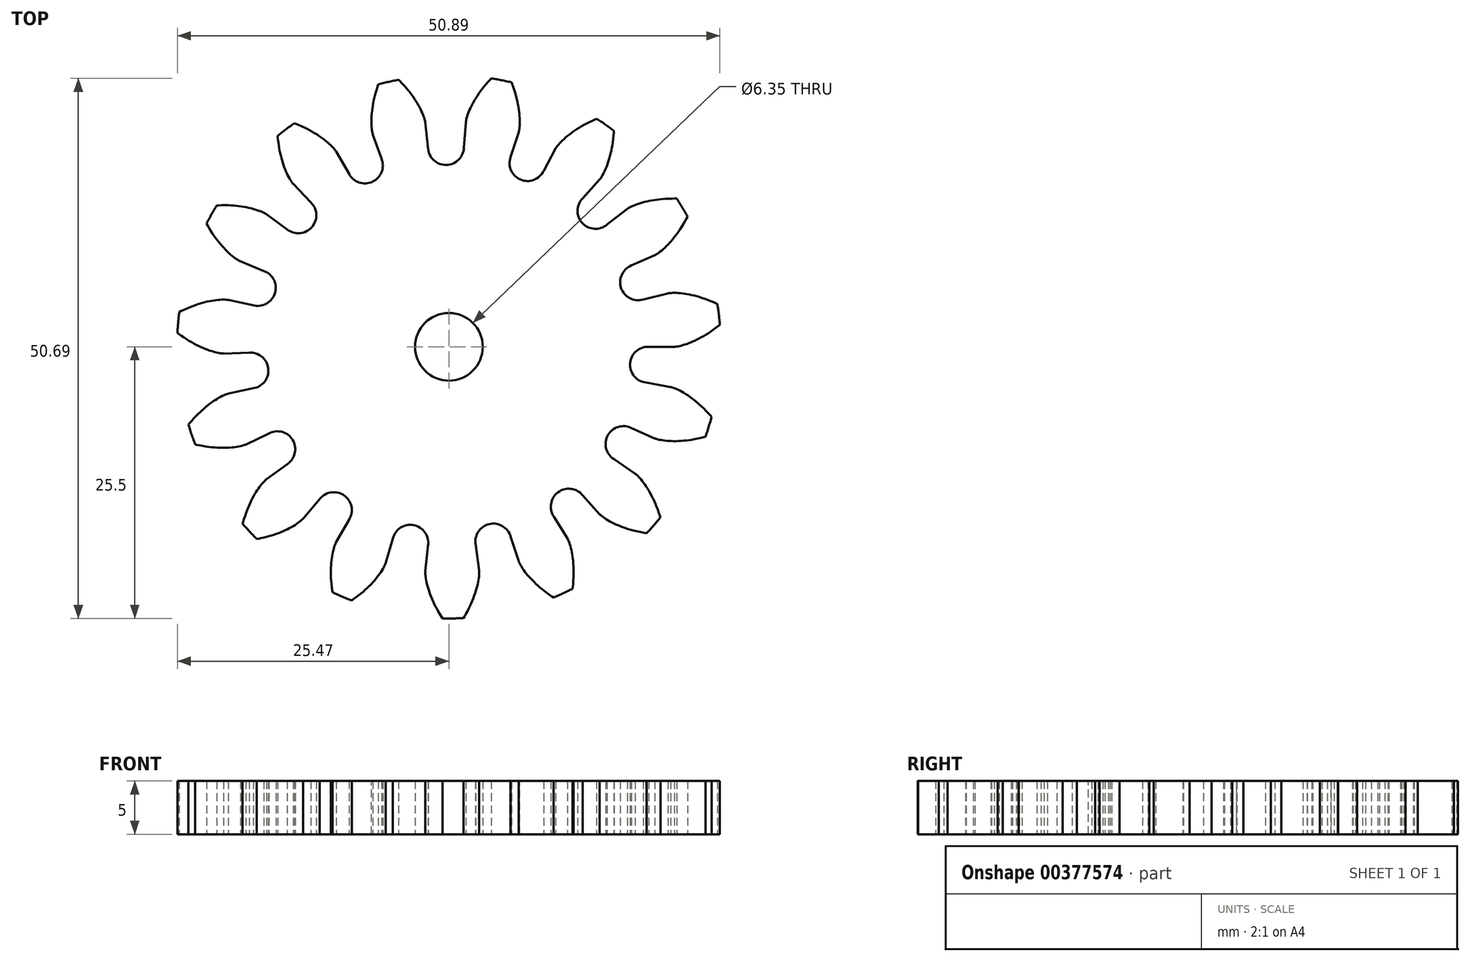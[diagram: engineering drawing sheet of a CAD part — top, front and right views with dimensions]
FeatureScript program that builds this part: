
annotation { "Feature Type Name" : "Feature", "Feature Type Description" : "" }
export const myFeature = defineFeature(function(context is Context, id is Id, definition is map)
    precondition{}
    {
        {
            assignVariable(context, id + "F0", {"name" : "T", "anyValue" : 15});
        }
        {
            var Q0;
            Q0=qCreatedBy(makeId("Top.planeOp"),FACE);
            var sketch = newSketch(context, id + "F1", { "sketchPlane" : qUnion([Q0])});
            skCircle(sketch, "E0", {"center": v(0, 0) * mm, "radius": 25.5 * mm});
            skCircle(sketch, "E1", {"center": v(0, 0) * mm, "radius": 22.5 * mm, "construction": true});
            skCircle(sketch, "E2", {"center": v(0, 0) * mm, "radius": 21.14 * mm, "construction": true});
            skCircle(sketch, "E3", {"center": v(0, 0) * mm, "radius": 18.75 * mm});
            skLineSegment(sketch, "E4", {"start": v(0, 0) * mm, "end": v(21.14, 0) * mm});
            skFitSpline(sketch, "E5", {"points": [v(21.14, 0) * mm, v(21.2, 0) * mm, v(21.38, 0.02) * mm, v(21.67, 0.08) * mm, v(22.07, 0.19) * mm, v(22.57, 0.36) * mm, v(23.17, 0.62) * mm, v(23.85, 0.98) * mm, v(24.6, 1.46) * mm, v(25.4, 2.06) * mm, v(26.26, 2.79) * mm], "startDerivative": vector(5.3, 0.26) * mm, "endDerivative": vector(17.52, 15.1) * mm});
            skLineSegment(sketch, "E6", {"start": v(0, 0) * mm, "end": v(25.4, -2.29) * mm, "construction": true});
            skLineSegment(sketch, "E7", {"start": v(0, 0) * mm, "end": v(22.5, 0.34) * mm, "construction": true});
            skFitSpline(sketch, "E8.MirrorCS", {"points": [v(20.8, -3.78) * mm, v(20.86, -3.8) * mm, v(21.03, -3.84) * mm, v(21.3, -3.95) * mm, v(21.68, -4.13) * mm, v(22.14, -4.4) * mm, v(22.68, -4.75) * mm, v(23.29, -5.23) * mm, v(23.94, -5.83) * mm, v(24.63, -6.56) * mm, v(25.34, -7.44) * mm], "startDerivative": vector(5.17, -1.2) * mm, "endDerivative": vector(14.54, -17.99) * mm});
            skLineSegment(sketch, "E9", {"start": v(0, 0) * mm, "end": v(20.8, -3.78) * mm});
            skSolve(sketch);
        }
        {
            var Q0;
            Q0=qCreatedBy(makeId("Top.planeOp"),FACE);
            var sketch = newSketch(context, id + "F2", { "sketchPlane" : qUnion([Q0])});
            skCircle(sketch, "E10", {"center": v(0, 0) * mm, "radius": 25.5 * mm});
            skSolve(sketch);
        }
        {
            var Q0;
            {var subQ0=sQuery(id+"F1.wireOp",EDGE,"E5");var subQ7=sQuery(id+"F1.wireOp",EDGE,"E0");var subQ8=makeQuery(id+"F1.imprint","INTERSECT",VERTEX,{"derivedFrom":[subQ7,subQ0]});Q0=makeQuery(id+"F1.imprint","IMPRINT",FACE,{"disambiguationData":[TD([[makeQuery(id+"F1.imprint","IMPRINT",EDGE,{"disambiguationData":[TD([[subQ8,1.0]])],"derivedFrom":subQ7}),1.0]])]});}
            extrude(context, id + "F3", {"entities" : qUnion([Q0]), "depth" : 6 * mm});
        }
        {
            var Q0;
            Q0=makeQuery(id+"F3.opExtrude","CAP_FACE",FACE,{"disambiguationData":[OSD([sQuery(id+"F1.wireOp",EDGE,"E0"),sQuery(id+"F1.wireOp",EDGE,"E3"),sQuery(id+"F1.wireOp",EDGE,"E4"),sQuery(id+"F1.wireOp",EDGE,"E5"),sQuery(id+"F1.wireOp",EDGE,"E8.MirrorCS"),sQuery(id+"F1.wireOp",EDGE,"E9")])],"isStart":true});
            var sketch = newSketch(context, id + "F4", { "sketchPlane" : qUnion([Q0])});
            skCircle(sketch, "E11", {"center": v(18.67, 1.68) * mm, "radius": 1.68 * mm});
            skSolve(sketch);
        }
        {
            var Q0;
            {var subQ1=makeQuery(id+"F3.opExtrude","CAP_EDGE",EDGE,{"disambiguationData":[OSD([sQuery(id+"F1.wireOp",EDGE,"E3")])],"isStart":true});Q0=makeQuery(id+"F4.imprint","IMPRINT",FACE,{"disambiguationData":[TD([[makeQuery(id+"F4.imprint","IMPRINT",EDGE,{"derivedFrom":subQ1}),-1.0]])]});}
            extrude(context, id + "F5", {"entities" : qUnion([Q0]), "operationType" : NewBodyOperationType.ADD, "oppositeDirection" : true, "depth" : 6 * mm});
        }
        {
            var Q0;
            Q0=makeQuery(id+"F2.imprint","IMPRINT",FACE,{"disambiguationData":[TD([[makeQuery(id+"F2.imprint","IMPRINT",EDGE,{"derivedFrom":sQuery(id+"F2.wireOp",EDGE,"E10")}),1.0]])]});
            extrude(context, id + "F6", {"entities" : qUnion([Q0]), "depth" : 5 * mm});
        }
        {
            var Q0;
            Q0=makeQuery(id+"F3.opExtrude","SWEPT_BODY",BODY,{"disambiguationData":[OSD([sQuery(id+"F1.wireOp",EDGE,"E0"),sQuery(id+"F1.wireOp",EDGE,"E3"),sQuery(id+"F1.wireOp",EDGE,"E4"),sQuery(id+"F1.wireOp",EDGE,"E5"),sQuery(id+"F1.wireOp",EDGE,"E8.MirrorCS"),sQuery(id+"F1.wireOp",EDGE,"E9")])]});
            var Q1;
            Q1=makeQuery(id+"F6.opExtrude","CAP_EDGE",EDGE,{"disambiguationData":[OSD([sQuery(id+"F2.wireOp",EDGE,"E10")])],"isStart":false});
            circularPattern(context, id + "F7", {"entities" : qUnion([Q0]), "axis" : qUnion([Q1]), "angle" : 360 * degree, "instanceCount" : getVariable(context, 'T'), "equalSpace" : true});
        }
        {
            var Q0;
            Q0=makeQuery(id+"F7.opPattern","COPY",BODY,{"derivedFrom":makeQuery(id+"F3.opExtrude","SWEPT_BODY",BODY,{"disambiguationData":[OSD([sQuery(id+"F1.wireOp",EDGE,"E0"),sQuery(id+"F1.wireOp",EDGE,"E3"),sQuery(id+"F1.wireOp",EDGE,"E4"),sQuery(id+"F1.wireOp",EDGE,"E5"),sQuery(id+"F1.wireOp",EDGE,"E8.MirrorCS"),sQuery(id+"F1.wireOp",EDGE,"E9")])]}),"instanceName":"5"});
            var Q1;
            Q1=makeQuery(id+"F7.opPattern","COPY",BODY,{"derivedFrom":makeQuery(id+"F3.opExtrude","SWEPT_BODY",BODY,{"disambiguationData":[OSD([sQuery(id+"F1.wireOp",EDGE,"E0"),sQuery(id+"F1.wireOp",EDGE,"E3"),sQuery(id+"F1.wireOp",EDGE,"E4"),sQuery(id+"F1.wireOp",EDGE,"E5"),sQuery(id+"F1.wireOp",EDGE,"E8.MirrorCS"),sQuery(id+"F1.wireOp",EDGE,"E9")])]}),"instanceName":"6"});
            var Q2;
            Q2=makeQuery(id+"F7.opPattern","COPY",BODY,{"derivedFrom":makeQuery(id+"F3.opExtrude","SWEPT_BODY",BODY,{"disambiguationData":[OSD([sQuery(id+"F1.wireOp",EDGE,"E0"),sQuery(id+"F1.wireOp",EDGE,"E3"),sQuery(id+"F1.wireOp",EDGE,"E4"),sQuery(id+"F1.wireOp",EDGE,"E5"),sQuery(id+"F1.wireOp",EDGE,"E8.MirrorCS"),sQuery(id+"F1.wireOp",EDGE,"E9")])]}),"instanceName":"7"});
            var Q3;
            Q3=makeQuery(id+"F7.opPattern","COPY",BODY,{"derivedFrom":makeQuery(id+"F3.opExtrude","SWEPT_BODY",BODY,{"disambiguationData":[OSD([sQuery(id+"F1.wireOp",EDGE,"E0"),sQuery(id+"F1.wireOp",EDGE,"E3"),sQuery(id+"F1.wireOp",EDGE,"E4"),sQuery(id+"F1.wireOp",EDGE,"E5"),sQuery(id+"F1.wireOp",EDGE,"E8.MirrorCS"),sQuery(id+"F1.wireOp",EDGE,"E9")])]}),"instanceName":"8"});
            var Q4;
            Q4=makeQuery(id+"F7.opPattern","COPY",BODY,{"derivedFrom":makeQuery(id+"F3.opExtrude","SWEPT_BODY",BODY,{"disambiguationData":[OSD([sQuery(id+"F1.wireOp",EDGE,"E0"),sQuery(id+"F1.wireOp",EDGE,"E3"),sQuery(id+"F1.wireOp",EDGE,"E4"),sQuery(id+"F1.wireOp",EDGE,"E5"),sQuery(id+"F1.wireOp",EDGE,"E8.MirrorCS"),sQuery(id+"F1.wireOp",EDGE,"E9")])]}),"instanceName":"9"});
            var Q5;
            Q5=makeQuery(id+"F7.opPattern","COPY",BODY,{"derivedFrom":makeQuery(id+"F3.opExtrude","SWEPT_BODY",BODY,{"disambiguationData":[OSD([sQuery(id+"F1.wireOp",EDGE,"E0"),sQuery(id+"F1.wireOp",EDGE,"E3"),sQuery(id+"F1.wireOp",EDGE,"E4"),sQuery(id+"F1.wireOp",EDGE,"E5"),sQuery(id+"F1.wireOp",EDGE,"E8.MirrorCS"),sQuery(id+"F1.wireOp",EDGE,"E9")])]}),"instanceName":"10"});
            var Q6;
            Q6=makeQuery(id+"F7.opPattern","COPY",BODY,{"derivedFrom":makeQuery(id+"F3.opExtrude","SWEPT_BODY",BODY,{"disambiguationData":[OSD([sQuery(id+"F1.wireOp",EDGE,"E0"),sQuery(id+"F1.wireOp",EDGE,"E3"),sQuery(id+"F1.wireOp",EDGE,"E4"),sQuery(id+"F1.wireOp",EDGE,"E5"),sQuery(id+"F1.wireOp",EDGE,"E8.MirrorCS"),sQuery(id+"F1.wireOp",EDGE,"E9")])]}),"instanceName":"11"});
            var Q7;
            Q7=makeQuery(id+"F7.opPattern","COPY",BODY,{"derivedFrom":makeQuery(id+"F3.opExtrude","SWEPT_BODY",BODY,{"disambiguationData":[OSD([sQuery(id+"F1.wireOp",EDGE,"E0"),sQuery(id+"F1.wireOp",EDGE,"E3"),sQuery(id+"F1.wireOp",EDGE,"E4"),sQuery(id+"F1.wireOp",EDGE,"E5"),sQuery(id+"F1.wireOp",EDGE,"E8.MirrorCS"),sQuery(id+"F1.wireOp",EDGE,"E9")])]}),"instanceName":"12"});
            var Q8;
            Q8=makeQuery(id+"F7.opPattern","COPY",BODY,{"derivedFrom":makeQuery(id+"F3.opExtrude","SWEPT_BODY",BODY,{"disambiguationData":[OSD([sQuery(id+"F1.wireOp",EDGE,"E0"),sQuery(id+"F1.wireOp",EDGE,"E3"),sQuery(id+"F1.wireOp",EDGE,"E4"),sQuery(id+"F1.wireOp",EDGE,"E5"),sQuery(id+"F1.wireOp",EDGE,"E8.MirrorCS"),sQuery(id+"F1.wireOp",EDGE,"E9")])]}),"instanceName":"13"});
            var Q9;
            Q9=makeQuery(id+"F7.opPattern","COPY",BODY,{"derivedFrom":makeQuery(id+"F3.opExtrude","SWEPT_BODY",BODY,{"disambiguationData":[OSD([sQuery(id+"F1.wireOp",EDGE,"E0"),sQuery(id+"F1.wireOp",EDGE,"E3"),sQuery(id+"F1.wireOp",EDGE,"E4"),sQuery(id+"F1.wireOp",EDGE,"E5"),sQuery(id+"F1.wireOp",EDGE,"E8.MirrorCS"),sQuery(id+"F1.wireOp",EDGE,"E9")])]}),"instanceName":"14"});
            var Q10;
            Q10=makeQuery(id+"F7.opPattern","COPY",BODY,{"derivedFrom":makeQuery(id+"F3.opExtrude","SWEPT_BODY",BODY,{"disambiguationData":[OSD([sQuery(id+"F1.wireOp",EDGE,"E0"),sQuery(id+"F1.wireOp",EDGE,"E3"),sQuery(id+"F1.wireOp",EDGE,"E4"),sQuery(id+"F1.wireOp",EDGE,"E5"),sQuery(id+"F1.wireOp",EDGE,"E8.MirrorCS"),sQuery(id+"F1.wireOp",EDGE,"E9")])]}),"instanceName":"15"});
            var Q11;
            Q11=makeQuery(id+"F7.opPattern","COPY",BODY,{"derivedFrom":makeQuery(id+"F3.opExtrude","SWEPT_BODY",BODY,{"disambiguationData":[OSD([sQuery(id+"F1.wireOp",EDGE,"E0"),sQuery(id+"F1.wireOp",EDGE,"E3"),sQuery(id+"F1.wireOp",EDGE,"E4"),sQuery(id+"F1.wireOp",EDGE,"E5"),sQuery(id+"F1.wireOp",EDGE,"E8.MirrorCS"),sQuery(id+"F1.wireOp",EDGE,"E9")])]}),"instanceName":"16"});
            var Q12;
            Q12=makeQuery(id+"F7.opPattern","COPY",BODY,{"derivedFrom":makeQuery(id+"F3.opExtrude","SWEPT_BODY",BODY,{"disambiguationData":[OSD([sQuery(id+"F1.wireOp",EDGE,"E0"),sQuery(id+"F1.wireOp",EDGE,"E3"),sQuery(id+"F1.wireOp",EDGE,"E4"),sQuery(id+"F1.wireOp",EDGE,"E5"),sQuery(id+"F1.wireOp",EDGE,"E8.MirrorCS"),sQuery(id+"F1.wireOp",EDGE,"E9")])]}),"instanceName":"17"});
            var Q13;
            Q13=makeQuery(id+"F7.opPattern","COPY",BODY,{"derivedFrom":makeQuery(id+"F3.opExtrude","SWEPT_BODY",BODY,{"disambiguationData":[OSD([sQuery(id+"F1.wireOp",EDGE,"E0"),sQuery(id+"F1.wireOp",EDGE,"E3"),sQuery(id+"F1.wireOp",EDGE,"E4"),sQuery(id+"F1.wireOp",EDGE,"E5"),sQuery(id+"F1.wireOp",EDGE,"E8.MirrorCS"),sQuery(id+"F1.wireOp",EDGE,"E9")])]}),"instanceName":"18"});
            var Q14;
            Q14=makeQuery(id+"F7.opPattern","COPY",BODY,{"derivedFrom":makeQuery(id+"F3.opExtrude","SWEPT_BODY",BODY,{"disambiguationData":[OSD([sQuery(id+"F1.wireOp",EDGE,"E0"),sQuery(id+"F1.wireOp",EDGE,"E3"),sQuery(id+"F1.wireOp",EDGE,"E4"),sQuery(id+"F1.wireOp",EDGE,"E5"),sQuery(id+"F1.wireOp",EDGE,"E8.MirrorCS"),sQuery(id+"F1.wireOp",EDGE,"E9")])]}),"instanceName":"19"});
            var Q15;
            Q15=makeQuery(id+"F7.opPattern","COPY",BODY,{"derivedFrom":makeQuery(id+"F3.opExtrude","SWEPT_BODY",BODY,{"disambiguationData":[OSD([sQuery(id+"F1.wireOp",EDGE,"E0"),sQuery(id+"F1.wireOp",EDGE,"E3"),sQuery(id+"F1.wireOp",EDGE,"E4"),sQuery(id+"F1.wireOp",EDGE,"E5"),sQuery(id+"F1.wireOp",EDGE,"E8.MirrorCS"),sQuery(id+"F1.wireOp",EDGE,"E9")])]}),"instanceName":"20"});
            var Q16;
            Q16=makeQuery(id+"F7.opPattern","COPY",BODY,{"derivedFrom":makeQuery(id+"F3.opExtrude","SWEPT_BODY",BODY,{"disambiguationData":[OSD([sQuery(id+"F1.wireOp",EDGE,"E0"),sQuery(id+"F1.wireOp",EDGE,"E3"),sQuery(id+"F1.wireOp",EDGE,"E4"),sQuery(id+"F1.wireOp",EDGE,"E5"),sQuery(id+"F1.wireOp",EDGE,"E8.MirrorCS"),sQuery(id+"F1.wireOp",EDGE,"E9")])]}),"instanceName":"21"});
            var Q17;
            Q17=makeQuery(id+"F7.opPattern","COPY",BODY,{"derivedFrom":makeQuery(id+"F3.opExtrude","SWEPT_BODY",BODY,{"disambiguationData":[OSD([sQuery(id+"F1.wireOp",EDGE,"E0"),sQuery(id+"F1.wireOp",EDGE,"E3"),sQuery(id+"F1.wireOp",EDGE,"E4"),sQuery(id+"F1.wireOp",EDGE,"E5"),sQuery(id+"F1.wireOp",EDGE,"E8.MirrorCS"),sQuery(id+"F1.wireOp",EDGE,"E9")])]}),"instanceName":"22"});
            var Q18;
            Q18=makeQuery(id+"F7.opPattern","COPY",BODY,{"derivedFrom":makeQuery(id+"F3.opExtrude","SWEPT_BODY",BODY,{"disambiguationData":[OSD([sQuery(id+"F1.wireOp",EDGE,"E0"),sQuery(id+"F1.wireOp",EDGE,"E3"),sQuery(id+"F1.wireOp",EDGE,"E4"),sQuery(id+"F1.wireOp",EDGE,"E5"),sQuery(id+"F1.wireOp",EDGE,"E8.MirrorCS"),sQuery(id+"F1.wireOp",EDGE,"E9")])]}),"instanceName":"23"});
            var Q19;
            Q19=makeQuery(id+"F7.opPattern","COPY",BODY,{"derivedFrom":makeQuery(id+"F3.opExtrude","SWEPT_BODY",BODY,{"disambiguationData":[OSD([sQuery(id+"F1.wireOp",EDGE,"E0"),sQuery(id+"F1.wireOp",EDGE,"E3"),sQuery(id+"F1.wireOp",EDGE,"E4"),sQuery(id+"F1.wireOp",EDGE,"E5"),sQuery(id+"F1.wireOp",EDGE,"E8.MirrorCS"),sQuery(id+"F1.wireOp",EDGE,"E9")])]}),"instanceName":"24"});
            var Q20;
            Q20=makeQuery(id+"F7.opPattern","COPY",BODY,{"derivedFrom":makeQuery(id+"F3.opExtrude","SWEPT_BODY",BODY,{"disambiguationData":[OSD([sQuery(id+"F1.wireOp",EDGE,"E0"),sQuery(id+"F1.wireOp",EDGE,"E3"),sQuery(id+"F1.wireOp",EDGE,"E4"),sQuery(id+"F1.wireOp",EDGE,"E5"),sQuery(id+"F1.wireOp",EDGE,"E8.MirrorCS"),sQuery(id+"F1.wireOp",EDGE,"E9")])]}),"instanceName":"25"});
            var Q21;
            Q21=makeQuery(id+"F7.opPattern","COPY",BODY,{"derivedFrom":makeQuery(id+"F3.opExtrude","SWEPT_BODY",BODY,{"disambiguationData":[OSD([sQuery(id+"F1.wireOp",EDGE,"E0"),sQuery(id+"F1.wireOp",EDGE,"E3"),sQuery(id+"F1.wireOp",EDGE,"E4"),sQuery(id+"F1.wireOp",EDGE,"E5"),sQuery(id+"F1.wireOp",EDGE,"E8.MirrorCS"),sQuery(id+"F1.wireOp",EDGE,"E9")])]}),"instanceName":"26"});
            var Q22;
            Q22=makeQuery(id+"F7.opPattern","COPY",BODY,{"derivedFrom":makeQuery(id+"F3.opExtrude","SWEPT_BODY",BODY,{"disambiguationData":[OSD([sQuery(id+"F1.wireOp",EDGE,"E0"),sQuery(id+"F1.wireOp",EDGE,"E3"),sQuery(id+"F1.wireOp",EDGE,"E4"),sQuery(id+"F1.wireOp",EDGE,"E5"),sQuery(id+"F1.wireOp",EDGE,"E8.MirrorCS"),sQuery(id+"F1.wireOp",EDGE,"E9")])]}),"instanceName":"27"});
            var Q23;
            Q23=makeQuery(id+"F7.opPattern","COPY",BODY,{"derivedFrom":makeQuery(id+"F3.opExtrude","SWEPT_BODY",BODY,{"disambiguationData":[OSD([sQuery(id+"F1.wireOp",EDGE,"E0"),sQuery(id+"F1.wireOp",EDGE,"E3"),sQuery(id+"F1.wireOp",EDGE,"E4"),sQuery(id+"F1.wireOp",EDGE,"E5"),sQuery(id+"F1.wireOp",EDGE,"E8.MirrorCS"),sQuery(id+"F1.wireOp",EDGE,"E9")])]}),"instanceName":"28"});
            var Q24;
            Q24=makeQuery(id+"F7.opPattern","COPY",BODY,{"derivedFrom":makeQuery(id+"F3.opExtrude","SWEPT_BODY",BODY,{"disambiguationData":[OSD([sQuery(id+"F1.wireOp",EDGE,"E0"),sQuery(id+"F1.wireOp",EDGE,"E3"),sQuery(id+"F1.wireOp",EDGE,"E4"),sQuery(id+"F1.wireOp",EDGE,"E5"),sQuery(id+"F1.wireOp",EDGE,"E8.MirrorCS"),sQuery(id+"F1.wireOp",EDGE,"E9")])]}),"instanceName":"29"});
            var Q25;
            Q25=makeQuery(id+"F3.opExtrude","SWEPT_BODY",BODY,{"disambiguationData":[OSD([sQuery(id+"F1.wireOp",EDGE,"E0"),sQuery(id+"F1.wireOp",EDGE,"E3"),sQuery(id+"F1.wireOp",EDGE,"E4"),sQuery(id+"F1.wireOp",EDGE,"E5"),sQuery(id+"F1.wireOp",EDGE,"E8.MirrorCS"),sQuery(id+"F1.wireOp",EDGE,"E9")])]});
            var Q26;
            Q26=makeQuery(id+"F7.opPattern","COPY",BODY,{"derivedFrom":makeQuery(id+"F3.opExtrude","SWEPT_BODY",BODY,{"disambiguationData":[OSD([sQuery(id+"F1.wireOp",EDGE,"E0"),sQuery(id+"F1.wireOp",EDGE,"E3"),sQuery(id+"F1.wireOp",EDGE,"E4"),sQuery(id+"F1.wireOp",EDGE,"E5"),sQuery(id+"F1.wireOp",EDGE,"E8.MirrorCS"),sQuery(id+"F1.wireOp",EDGE,"E9")])]}),"instanceName":"1"});
            var Q27;
            Q27=makeQuery(id+"F7.opPattern","COPY",BODY,{"derivedFrom":makeQuery(id+"F3.opExtrude","SWEPT_BODY",BODY,{"disambiguationData":[OSD([sQuery(id+"F1.wireOp",EDGE,"E0"),sQuery(id+"F1.wireOp",EDGE,"E3"),sQuery(id+"F1.wireOp",EDGE,"E4"),sQuery(id+"F1.wireOp",EDGE,"E5"),sQuery(id+"F1.wireOp",EDGE,"E8.MirrorCS"),sQuery(id+"F1.wireOp",EDGE,"E9")])]}),"instanceName":"2"});
            var Q28;
            Q28=makeQuery(id+"F7.opPattern","COPY",BODY,{"derivedFrom":makeQuery(id+"F3.opExtrude","SWEPT_BODY",BODY,{"disambiguationData":[OSD([sQuery(id+"F1.wireOp",EDGE,"E0"),sQuery(id+"F1.wireOp",EDGE,"E3"),sQuery(id+"F1.wireOp",EDGE,"E4"),sQuery(id+"F1.wireOp",EDGE,"E5"),sQuery(id+"F1.wireOp",EDGE,"E8.MirrorCS"),sQuery(id+"F1.wireOp",EDGE,"E9")])]}),"instanceName":"3"});
            var Q29;
            Q29=makeQuery(id+"F7.opPattern","COPY",BODY,{"derivedFrom":makeQuery(id+"F3.opExtrude","SWEPT_BODY",BODY,{"disambiguationData":[OSD([sQuery(id+"F1.wireOp",EDGE,"E0"),sQuery(id+"F1.wireOp",EDGE,"E3"),sQuery(id+"F1.wireOp",EDGE,"E4"),sQuery(id+"F1.wireOp",EDGE,"E5"),sQuery(id+"F1.wireOp",EDGE,"E8.MirrorCS"),sQuery(id+"F1.wireOp",EDGE,"E9")])]}),"instanceName":"4"});
            var Q30;
            Q30=makeQuery(id+"F7.opPattern","COPY",BODY,{"derivedFrom":makeQuery(id+"F3.opExtrude","SWEPT_BODY",BODY,{"disambiguationData":[OSD([sQuery(id+"F1.wireOp",EDGE,"E0"),sQuery(id+"F1.wireOp",EDGE,"E3"),sQuery(id+"F1.wireOp",EDGE,"E5"),sQuery(id+"F1.wireOp",EDGE,"E8.MirrorCS")])]}),"instanceName":"30"});
            var Q31;
            Q31=makeQuery(id+"F7.opPattern","COPY",BODY,{"derivedFrom":makeQuery(id+"F3.opExtrude","SWEPT_BODY",BODY,{"disambiguationData":[OSD([sQuery(id+"F1.wireOp",EDGE,"E0"),sQuery(id+"F1.wireOp",EDGE,"E3"),sQuery(id+"F1.wireOp",EDGE,"E5"),sQuery(id+"F1.wireOp",EDGE,"E8.MirrorCS")])]}),"instanceName":"31"});
            var Q32;
            Q32=makeQuery(id+"F7.opPattern","COPY",BODY,{"derivedFrom":makeQuery(id+"F3.opExtrude","SWEPT_BODY",BODY,{"disambiguationData":[OSD([sQuery(id+"F1.wireOp",EDGE,"E0"),sQuery(id+"F1.wireOp",EDGE,"E3"),sQuery(id+"F1.wireOp",EDGE,"E5"),sQuery(id+"F1.wireOp",EDGE,"E8.MirrorCS")])]}),"instanceName":"32"});
            var Q33;
            Q33=makeQuery(id+"F7.opPattern","COPY",BODY,{"derivedFrom":makeQuery(id+"F3.opExtrude","SWEPT_BODY",BODY,{"disambiguationData":[OSD([sQuery(id+"F1.wireOp",EDGE,"E0"),sQuery(id+"F1.wireOp",EDGE,"E3"),sQuery(id+"F1.wireOp",EDGE,"E5"),sQuery(id+"F1.wireOp",EDGE,"E8.MirrorCS")])]}),"instanceName":"33"});
            var Q34;
            Q34=makeQuery(id+"F7.opPattern","COPY",BODY,{"derivedFrom":makeQuery(id+"F3.opExtrude","SWEPT_BODY",BODY,{"disambiguationData":[OSD([sQuery(id+"F1.wireOp",EDGE,"E0"),sQuery(id+"F1.wireOp",EDGE,"E3"),sQuery(id+"F1.wireOp",EDGE,"E5"),sQuery(id+"F1.wireOp",EDGE,"E8.MirrorCS")])]}),"instanceName":"34"});
            var Q35;
            Q35=makeQuery(id+"F7.opPattern","COPY",BODY,{"derivedFrom":makeQuery(id+"F3.opExtrude","SWEPT_BODY",BODY,{"disambiguationData":[OSD([sQuery(id+"F1.wireOp",EDGE,"E0"),sQuery(id+"F1.wireOp",EDGE,"E3"),sQuery(id+"F1.wireOp",EDGE,"E5"),sQuery(id+"F1.wireOp",EDGE,"E8.MirrorCS")])]}),"instanceName":"35"});
            var Q36;
            Q36=makeQuery(id+"F7.opPattern","COPY",BODY,{"derivedFrom":makeQuery(id+"F3.opExtrude","SWEPT_BODY",BODY,{"disambiguationData":[OSD([sQuery(id+"F1.wireOp",EDGE,"E0"),sQuery(id+"F1.wireOp",EDGE,"E3"),sQuery(id+"F1.wireOp",EDGE,"E5"),sQuery(id+"F1.wireOp",EDGE,"E8.MirrorCS")])]}),"instanceName":"36"});
            var Q37;
            Q37=makeQuery(id+"F7.opPattern","COPY",BODY,{"derivedFrom":makeQuery(id+"F3.opExtrude","SWEPT_BODY",BODY,{"disambiguationData":[OSD([sQuery(id+"F1.wireOp",EDGE,"E0"),sQuery(id+"F1.wireOp",EDGE,"E3"),sQuery(id+"F1.wireOp",EDGE,"E5"),sQuery(id+"F1.wireOp",EDGE,"E8.MirrorCS")])]}),"instanceName":"37"});
            var Q38;
            Q38=makeQuery(id+"F7.opPattern","COPY",BODY,{"derivedFrom":makeQuery(id+"F3.opExtrude","SWEPT_BODY",BODY,{"disambiguationData":[OSD([sQuery(id+"F1.wireOp",EDGE,"E0"),sQuery(id+"F1.wireOp",EDGE,"E3"),sQuery(id+"F1.wireOp",EDGE,"E5"),sQuery(id+"F1.wireOp",EDGE,"E8.MirrorCS")])]}),"instanceName":"38"});
            var Q39;
            Q39=makeQuery(id+"F7.opPattern","COPY",BODY,{"derivedFrom":makeQuery(id+"F3.opExtrude","SWEPT_BODY",BODY,{"disambiguationData":[OSD([sQuery(id+"F1.wireOp",EDGE,"E0"),sQuery(id+"F1.wireOp",EDGE,"E3"),sQuery(id+"F1.wireOp",EDGE,"E5"),sQuery(id+"F1.wireOp",EDGE,"E8.MirrorCS")])]}),"instanceName":"39"});
            var Q40;
            Q40=makeQuery(id+"F7.opPattern","COPY",BODY,{"derivedFrom":makeQuery(id+"F3.opExtrude","SWEPT_BODY",BODY,{"disambiguationData":[OSD([sQuery(id+"F1.wireOp",EDGE,"E0"),sQuery(id+"F1.wireOp",EDGE,"E3"),sQuery(id+"F1.wireOp",EDGE,"E5"),sQuery(id+"F1.wireOp",EDGE,"E8.MirrorCS")])]}),"instanceName":"40"});
            var Q41;
            Q41=makeQuery(id+"F7.opPattern","COPY",BODY,{"derivedFrom":makeQuery(id+"F3.opExtrude","SWEPT_BODY",BODY,{"disambiguationData":[OSD([sQuery(id+"F1.wireOp",EDGE,"E0"),sQuery(id+"F1.wireOp",EDGE,"E3"),sQuery(id+"F1.wireOp",EDGE,"E5"),sQuery(id+"F1.wireOp",EDGE,"E8.MirrorCS")])]}),"instanceName":"41"});
            var Q42;
            Q42=makeQuery(id+"F7.opPattern","COPY",BODY,{"derivedFrom":makeQuery(id+"F3.opExtrude","SWEPT_BODY",BODY,{"disambiguationData":[OSD([sQuery(id+"F1.wireOp",EDGE,"E0"),sQuery(id+"F1.wireOp",EDGE,"E3"),sQuery(id+"F1.wireOp",EDGE,"E5"),sQuery(id+"F1.wireOp",EDGE,"E8.MirrorCS")])]}),"instanceName":"42"});
            var Q43;
            Q43=makeQuery(id+"F7.opPattern","COPY",BODY,{"derivedFrom":makeQuery(id+"F3.opExtrude","SWEPT_BODY",BODY,{"disambiguationData":[OSD([sQuery(id+"F1.wireOp",EDGE,"E0"),sQuery(id+"F1.wireOp",EDGE,"E3"),sQuery(id+"F1.wireOp",EDGE,"E5"),sQuery(id+"F1.wireOp",EDGE,"E8.MirrorCS")])]}),"instanceName":"43"});
            var Q44;
            Q44=makeQuery(id+"F7.opPattern","COPY",BODY,{"derivedFrom":makeQuery(id+"F3.opExtrude","SWEPT_BODY",BODY,{"disambiguationData":[OSD([sQuery(id+"F1.wireOp",EDGE,"E0"),sQuery(id+"F1.wireOp",EDGE,"E3"),sQuery(id+"F1.wireOp",EDGE,"E5"),sQuery(id+"F1.wireOp",EDGE,"E8.MirrorCS")])]}),"instanceName":"44"});
            var Q45;
            Q45=makeQuery(id+"F7.opPattern","COPY",BODY,{"derivedFrom":makeQuery(id+"F3.opExtrude","SWEPT_BODY",BODY,{"disambiguationData":[OSD([sQuery(id+"F1.wireOp",EDGE,"E0"),sQuery(id+"F1.wireOp",EDGE,"E3"),sQuery(id+"F1.wireOp",EDGE,"E5"),sQuery(id+"F1.wireOp",EDGE,"E8.MirrorCS")])]}),"instanceName":"45"});
            var Q46;
            Q46=makeQuery(id+"F7.opPattern","COPY",BODY,{"derivedFrom":makeQuery(id+"F3.opExtrude","SWEPT_BODY",BODY,{"disambiguationData":[OSD([sQuery(id+"F1.wireOp",EDGE,"E0"),sQuery(id+"F1.wireOp",EDGE,"E3"),sQuery(id+"F1.wireOp",EDGE,"E5"),sQuery(id+"F1.wireOp",EDGE,"E8.MirrorCS")])]}),"instanceName":"46"});
            var Q47;
            Q47=makeQuery(id+"F7.opPattern","COPY",BODY,{"derivedFrom":makeQuery(id+"F3.opExtrude","SWEPT_BODY",BODY,{"disambiguationData":[OSD([sQuery(id+"F1.wireOp",EDGE,"E0"),sQuery(id+"F1.wireOp",EDGE,"E3"),sQuery(id+"F1.wireOp",EDGE,"E5"),sQuery(id+"F1.wireOp",EDGE,"E8.MirrorCS")])]}),"instanceName":"47"});
            var Q48;
            Q48=makeQuery(id+"F7.opPattern","COPY",BODY,{"derivedFrom":makeQuery(id+"F3.opExtrude","SWEPT_BODY",BODY,{"disambiguationData":[OSD([sQuery(id+"F1.wireOp",EDGE,"E0"),sQuery(id+"F1.wireOp",EDGE,"E3"),sQuery(id+"F1.wireOp",EDGE,"E5"),sQuery(id+"F1.wireOp",EDGE,"E8.MirrorCS")])]}),"instanceName":"48"});
            var Q49;
            Q49=makeQuery(id+"F7.opPattern","COPY",BODY,{"derivedFrom":makeQuery(id+"F3.opExtrude","SWEPT_BODY",BODY,{"disambiguationData":[OSD([sQuery(id+"F1.wireOp",EDGE,"E0"),sQuery(id+"F1.wireOp",EDGE,"E3"),sQuery(id+"F1.wireOp",EDGE,"E5"),sQuery(id+"F1.wireOp",EDGE,"E8.MirrorCS")])]}),"instanceName":"49"});
            var Q50;
            Q50=makeQuery(id+"F7.opPattern","COPY",BODY,{"derivedFrom":makeQuery(id+"F3.opExtrude","SWEPT_BODY",BODY,{"disambiguationData":[OSD([sQuery(id+"F1.wireOp",EDGE,"E0"),sQuery(id+"F1.wireOp",EDGE,"E3"),sQuery(id+"F1.wireOp",EDGE,"E5"),sQuery(id+"F1.wireOp",EDGE,"E8.MirrorCS")])]}),"instanceName":"50"});
            var Q51;
            Q51=makeQuery(id+"F7.opPattern","COPY",BODY,{"derivedFrom":makeQuery(id+"F3.opExtrude","SWEPT_BODY",BODY,{"disambiguationData":[OSD([sQuery(id+"F1.wireOp",EDGE,"E0"),sQuery(id+"F1.wireOp",EDGE,"E3"),sQuery(id+"F1.wireOp",EDGE,"E5"),sQuery(id+"F1.wireOp",EDGE,"E8.MirrorCS")])]}),"instanceName":"51"});
            var Q52;
            Q52=makeQuery(id+"F7.opPattern","COPY",BODY,{"derivedFrom":makeQuery(id+"F3.opExtrude","SWEPT_BODY",BODY,{"disambiguationData":[OSD([sQuery(id+"F1.wireOp",EDGE,"E0"),sQuery(id+"F1.wireOp",EDGE,"E3"),sQuery(id+"F1.wireOp",EDGE,"E5"),sQuery(id+"F1.wireOp",EDGE,"E8.MirrorCS")])]}),"instanceName":"52"});
            var Q53;
            Q53=makeQuery(id+"F7.opPattern","COPY",BODY,{"derivedFrom":makeQuery(id+"F3.opExtrude","SWEPT_BODY",BODY,{"disambiguationData":[OSD([sQuery(id+"F1.wireOp",EDGE,"E0"),sQuery(id+"F1.wireOp",EDGE,"E3"),sQuery(id+"F1.wireOp",EDGE,"E5"),sQuery(id+"F1.wireOp",EDGE,"E8.MirrorCS")])]}),"instanceName":"53"});
            var Q54;
            Q54=makeQuery(id+"F7.opPattern","COPY",BODY,{"derivedFrom":makeQuery(id+"F3.opExtrude","SWEPT_BODY",BODY,{"disambiguationData":[OSD([sQuery(id+"F1.wireOp",EDGE,"E0"),sQuery(id+"F1.wireOp",EDGE,"E3"),sQuery(id+"F1.wireOp",EDGE,"E5"),sQuery(id+"F1.wireOp",EDGE,"E8.MirrorCS")])]}),"instanceName":"54"});
            var Q55;
            Q55=makeQuery(id+"F7.opPattern","COPY",BODY,{"derivedFrom":makeQuery(id+"F3.opExtrude","SWEPT_BODY",BODY,{"disambiguationData":[OSD([sQuery(id+"F1.wireOp",EDGE,"E0"),sQuery(id+"F1.wireOp",EDGE,"E3"),sQuery(id+"F1.wireOp",EDGE,"E5"),sQuery(id+"F1.wireOp",EDGE,"E8.MirrorCS")])]}),"instanceName":"55"});
            var Q56;
            Q56=makeQuery(id+"F7.opPattern","COPY",BODY,{"derivedFrom":makeQuery(id+"F3.opExtrude","SWEPT_BODY",BODY,{"disambiguationData":[OSD([sQuery(id+"F1.wireOp",EDGE,"E0"),sQuery(id+"F1.wireOp",EDGE,"E3"),sQuery(id+"F1.wireOp",EDGE,"E5"),sQuery(id+"F1.wireOp",EDGE,"E8.MirrorCS")])]}),"instanceName":"56"});
            var Q57;
            Q57=makeQuery(id+"F7.opPattern","COPY",BODY,{"derivedFrom":makeQuery(id+"F3.opExtrude","SWEPT_BODY",BODY,{"disambiguationData":[OSD([sQuery(id+"F1.wireOp",EDGE,"E0"),sQuery(id+"F1.wireOp",EDGE,"E3"),sQuery(id+"F1.wireOp",EDGE,"E5"),sQuery(id+"F1.wireOp",EDGE,"E8.MirrorCS")])]}),"instanceName":"57"});
            var Q58;
            Q58=makeQuery(id+"F7.opPattern","COPY",BODY,{"derivedFrom":makeQuery(id+"F3.opExtrude","SWEPT_BODY",BODY,{"disambiguationData":[OSD([sQuery(id+"F1.wireOp",EDGE,"E0"),sQuery(id+"F1.wireOp",EDGE,"E3"),sQuery(id+"F1.wireOp",EDGE,"E5"),sQuery(id+"F1.wireOp",EDGE,"E8.MirrorCS")])]}),"instanceName":"58"});
            var Q59;
            Q59=makeQuery(id+"F7.opPattern","COPY",BODY,{"derivedFrom":makeQuery(id+"F3.opExtrude","SWEPT_BODY",BODY,{"disambiguationData":[OSD([sQuery(id+"F1.wireOp",EDGE,"E0"),sQuery(id+"F1.wireOp",EDGE,"E3"),sQuery(id+"F1.wireOp",EDGE,"E5"),sQuery(id+"F1.wireOp",EDGE,"E8.MirrorCS")])]}),"instanceName":"59"});
            var Q60;
            Q60=makeQuery(id+"F7.opPattern","COPY",BODY,{"derivedFrom":makeQuery(id+"F3.opExtrude","SWEPT_BODY",BODY,{"disambiguationData":[OSD([sQuery(id+"F1.wireOp",EDGE,"E0"),sQuery(id+"F1.wireOp",EDGE,"E3"),sQuery(id+"F1.wireOp",EDGE,"E5"),sQuery(id+"F1.wireOp",EDGE,"E8.MirrorCS")])]}),"instanceName":"60"});
            var Q61;
            Q61=makeQuery(id+"F7.opPattern","COPY",BODY,{"derivedFrom":makeQuery(id+"F3.opExtrude","SWEPT_BODY",BODY,{"disambiguationData":[OSD([sQuery(id+"F1.wireOp",EDGE,"E0"),sQuery(id+"F1.wireOp",EDGE,"E3"),sQuery(id+"F1.wireOp",EDGE,"E5"),sQuery(id+"F1.wireOp",EDGE,"E8.MirrorCS")])]}),"instanceName":"61"});
            var Q62;
            Q62=makeQuery(id+"F7.opPattern","COPY",BODY,{"derivedFrom":makeQuery(id+"F3.opExtrude","SWEPT_BODY",BODY,{"disambiguationData":[OSD([sQuery(id+"F1.wireOp",EDGE,"E0"),sQuery(id+"F1.wireOp",EDGE,"E3"),sQuery(id+"F1.wireOp",EDGE,"E5"),sQuery(id+"F1.wireOp",EDGE,"E8.MirrorCS")])]}),"instanceName":"62"});
            var Q63;
            Q63=makeQuery(id+"F7.opPattern","COPY",BODY,{"derivedFrom":makeQuery(id+"F3.opExtrude","SWEPT_BODY",BODY,{"disambiguationData":[OSD([sQuery(id+"F1.wireOp",EDGE,"E0"),sQuery(id+"F1.wireOp",EDGE,"E3"),sQuery(id+"F1.wireOp",EDGE,"E5"),sQuery(id+"F1.wireOp",EDGE,"E8.MirrorCS")])]}),"instanceName":"63"});
            var Q64;
            Q64=makeQuery(id+"F7.opPattern","COPY",BODY,{"derivedFrom":makeQuery(id+"F3.opExtrude","SWEPT_BODY",BODY,{"disambiguationData":[OSD([sQuery(id+"F1.wireOp",EDGE,"E0"),sQuery(id+"F1.wireOp",EDGE,"E3"),sQuery(id+"F1.wireOp",EDGE,"E5"),sQuery(id+"F1.wireOp",EDGE,"E8.MirrorCS")])]}),"instanceName":"64"});
            var Q65;
            Q65=makeQuery(id+"F7.opPattern","COPY",BODY,{"derivedFrom":makeQuery(id+"F3.opExtrude","SWEPT_BODY",BODY,{"disambiguationData":[OSD([sQuery(id+"F1.wireOp",EDGE,"E0"),sQuery(id+"F1.wireOp",EDGE,"E3"),sQuery(id+"F1.wireOp",EDGE,"E5"),sQuery(id+"F1.wireOp",EDGE,"E8.MirrorCS")])]}),"instanceName":"65"});
            var Q66;
            Q66=makeQuery(id+"F7.opPattern","COPY",BODY,{"derivedFrom":makeQuery(id+"F3.opExtrude","SWEPT_BODY",BODY,{"disambiguationData":[OSD([sQuery(id+"F1.wireOp",EDGE,"E0"),sQuery(id+"F1.wireOp",EDGE,"E3"),sQuery(id+"F1.wireOp",EDGE,"E5"),sQuery(id+"F1.wireOp",EDGE,"E8.MirrorCS")])]}),"instanceName":"66"});
            var Q67;
            Q67=makeQuery(id+"F7.opPattern","COPY",BODY,{"derivedFrom":makeQuery(id+"F3.opExtrude","SWEPT_BODY",BODY,{"disambiguationData":[OSD([sQuery(id+"F1.wireOp",EDGE,"E0"),sQuery(id+"F1.wireOp",EDGE,"E3"),sQuery(id+"F1.wireOp",EDGE,"E5"),sQuery(id+"F1.wireOp",EDGE,"E8.MirrorCS")])]}),"instanceName":"67"});
            var Q68;
            Q68=makeQuery(id+"F7.opPattern","COPY",BODY,{"derivedFrom":makeQuery(id+"F3.opExtrude","SWEPT_BODY",BODY,{"disambiguationData":[OSD([sQuery(id+"F1.wireOp",EDGE,"E0"),sQuery(id+"F1.wireOp",EDGE,"E3"),sQuery(id+"F1.wireOp",EDGE,"E5"),sQuery(id+"F1.wireOp",EDGE,"E8.MirrorCS")])]}),"instanceName":"68"});
            var Q69;
            Q69=makeQuery(id+"F7.opPattern","COPY",BODY,{"derivedFrom":makeQuery(id+"F3.opExtrude","SWEPT_BODY",BODY,{"disambiguationData":[OSD([sQuery(id+"F1.wireOp",EDGE,"E0"),sQuery(id+"F1.wireOp",EDGE,"E3"),sQuery(id+"F1.wireOp",EDGE,"E5"),sQuery(id+"F1.wireOp",EDGE,"E8.MirrorCS")])]}),"instanceName":"69"});
            var Q70;
            Q70=makeQuery(id+"F7.opPattern","COPY",BODY,{"derivedFrom":makeQuery(id+"F3.opExtrude","SWEPT_BODY",BODY,{"disambiguationData":[OSD([sQuery(id+"F1.wireOp",EDGE,"E0"),sQuery(id+"F1.wireOp",EDGE,"E3"),sQuery(id+"F1.wireOp",EDGE,"E5"),sQuery(id+"F1.wireOp",EDGE,"E8.MirrorCS")])]}),"instanceName":"70"});
            var Q71;
            Q71=makeQuery(id+"F7.opPattern","COPY",BODY,{"derivedFrom":makeQuery(id+"F3.opExtrude","SWEPT_BODY",BODY,{"disambiguationData":[OSD([sQuery(id+"F1.wireOp",EDGE,"E0"),sQuery(id+"F1.wireOp",EDGE,"E3"),sQuery(id+"F1.wireOp",EDGE,"E5"),sQuery(id+"F1.wireOp",EDGE,"E8.MirrorCS")])]}),"instanceName":"71"});
            var Q72;
            Q72=makeQuery(id+"F7.opPattern","COPY",BODY,{"derivedFrom":makeQuery(id+"F3.opExtrude","SWEPT_BODY",BODY,{"disambiguationData":[OSD([sQuery(id+"F1.wireOp",EDGE,"E0"),sQuery(id+"F1.wireOp",EDGE,"E3"),sQuery(id+"F1.wireOp",EDGE,"E5"),sQuery(id+"F1.wireOp",EDGE,"E8.MirrorCS")])]}),"instanceName":"72"});
            var Q73;
            Q73=makeQuery(id+"F7.opPattern","COPY",BODY,{"derivedFrom":makeQuery(id+"F3.opExtrude","SWEPT_BODY",BODY,{"disambiguationData":[OSD([sQuery(id+"F1.wireOp",EDGE,"E0"),sQuery(id+"F1.wireOp",EDGE,"E3"),sQuery(id+"F1.wireOp",EDGE,"E5"),sQuery(id+"F1.wireOp",EDGE,"E8.MirrorCS")])]}),"instanceName":"73"});
            var Q74;
            Q74=makeQuery(id+"F7.opPattern","COPY",BODY,{"derivedFrom":makeQuery(id+"F3.opExtrude","SWEPT_BODY",BODY,{"disambiguationData":[OSD([sQuery(id+"F1.wireOp",EDGE,"E0"),sQuery(id+"F1.wireOp",EDGE,"E3"),sQuery(id+"F1.wireOp",EDGE,"E5"),sQuery(id+"F1.wireOp",EDGE,"E8.MirrorCS")])]}),"instanceName":"74"});
            var Q75;
            Q75=makeQuery(id+"F7.opPattern","COPY",BODY,{"derivedFrom":makeQuery(id+"F3.opExtrude","SWEPT_BODY",BODY,{"disambiguationData":[OSD([sQuery(id+"F1.wireOp",EDGE,"E0"),sQuery(id+"F1.wireOp",EDGE,"E3"),sQuery(id+"F1.wireOp",EDGE,"E5"),sQuery(id+"F1.wireOp",EDGE,"E8.MirrorCS")])]}),"instanceName":"75"});
            var Q76;
            Q76=makeQuery(id+"F7.opPattern","COPY",BODY,{"derivedFrom":makeQuery(id+"F3.opExtrude","SWEPT_BODY",BODY,{"disambiguationData":[OSD([sQuery(id+"F1.wireOp",EDGE,"E0"),sQuery(id+"F1.wireOp",EDGE,"E3"),sQuery(id+"F1.wireOp",EDGE,"E5"),sQuery(id+"F1.wireOp",EDGE,"E8.MirrorCS")])]}),"instanceName":"76"});
            var Q77;
            Q77=makeQuery(id+"F7.opPattern","COPY",BODY,{"derivedFrom":makeQuery(id+"F3.opExtrude","SWEPT_BODY",BODY,{"disambiguationData":[OSD([sQuery(id+"F1.wireOp",EDGE,"E0"),sQuery(id+"F1.wireOp",EDGE,"E3"),sQuery(id+"F1.wireOp",EDGE,"E5"),sQuery(id+"F1.wireOp",EDGE,"E8.MirrorCS")])]}),"instanceName":"77"});
            var Q78;
            Q78=makeQuery(id+"F7.opPattern","COPY",BODY,{"derivedFrom":makeQuery(id+"F3.opExtrude","SWEPT_BODY",BODY,{"disambiguationData":[OSD([sQuery(id+"F1.wireOp",EDGE,"E0"),sQuery(id+"F1.wireOp",EDGE,"E3"),sQuery(id+"F1.wireOp",EDGE,"E5"),sQuery(id+"F1.wireOp",EDGE,"E8.MirrorCS")])]}),"instanceName":"78"});
            var Q79;
            Q79=makeQuery(id+"F7.opPattern","COPY",BODY,{"derivedFrom":makeQuery(id+"F3.opExtrude","SWEPT_BODY",BODY,{"disambiguationData":[OSD([sQuery(id+"F1.wireOp",EDGE,"E0"),sQuery(id+"F1.wireOp",EDGE,"E3"),sQuery(id+"F1.wireOp",EDGE,"E5"),sQuery(id+"F1.wireOp",EDGE,"E8.MirrorCS")])]}),"instanceName":"79"});
            var Q80;
            Q80=makeQuery(id+"F7.opPattern","COPY",BODY,{"derivedFrom":makeQuery(id+"F3.opExtrude","SWEPT_BODY",BODY,{"disambiguationData":[OSD([sQuery(id+"F1.wireOp",EDGE,"E0"),sQuery(id+"F1.wireOp",EDGE,"E3"),sQuery(id+"F1.wireOp",EDGE,"E5"),sQuery(id+"F1.wireOp",EDGE,"E8.MirrorCS")])]}),"instanceName":"80"});
            var Q81;
            Q81=makeQuery(id+"F7.opPattern","COPY",BODY,{"derivedFrom":makeQuery(id+"F3.opExtrude","SWEPT_BODY",BODY,{"disambiguationData":[OSD([sQuery(id+"F1.wireOp",EDGE,"E0"),sQuery(id+"F1.wireOp",EDGE,"E3"),sQuery(id+"F1.wireOp",EDGE,"E5"),sQuery(id+"F1.wireOp",EDGE,"E8.MirrorCS")])]}),"instanceName":"81"});
            var Q82;
            Q82=makeQuery(id+"F7.opPattern","COPY",BODY,{"derivedFrom":makeQuery(id+"F3.opExtrude","SWEPT_BODY",BODY,{"disambiguationData":[OSD([sQuery(id+"F1.wireOp",EDGE,"E0"),sQuery(id+"F1.wireOp",EDGE,"E3"),sQuery(id+"F1.wireOp",EDGE,"E5"),sQuery(id+"F1.wireOp",EDGE,"E8.MirrorCS")])]}),"instanceName":"82"});
            var Q83;
            Q83=makeQuery(id+"F7.opPattern","COPY",BODY,{"derivedFrom":makeQuery(id+"F3.opExtrude","SWEPT_BODY",BODY,{"disambiguationData":[OSD([sQuery(id+"F1.wireOp",EDGE,"E0"),sQuery(id+"F1.wireOp",EDGE,"E3"),sQuery(id+"F1.wireOp",EDGE,"E5"),sQuery(id+"F1.wireOp",EDGE,"E8.MirrorCS")])]}),"instanceName":"83"});
            var Q84;
            Q84=makeQuery(id+"F7.opPattern","COPY",BODY,{"derivedFrom":makeQuery(id+"F3.opExtrude","SWEPT_BODY",BODY,{"disambiguationData":[OSD([sQuery(id+"F1.wireOp",EDGE,"E0"),sQuery(id+"F1.wireOp",EDGE,"E3"),sQuery(id+"F1.wireOp",EDGE,"E5"),sQuery(id+"F1.wireOp",EDGE,"E8.MirrorCS")])]}),"instanceName":"84"});
            var Q85;
            Q85=makeQuery(id+"F7.opPattern","COPY",BODY,{"derivedFrom":makeQuery(id+"F3.opExtrude","SWEPT_BODY",BODY,{"disambiguationData":[OSD([sQuery(id+"F1.wireOp",EDGE,"E0"),sQuery(id+"F1.wireOp",EDGE,"E3"),sQuery(id+"F1.wireOp",EDGE,"E5"),sQuery(id+"F1.wireOp",EDGE,"E8.MirrorCS")])]}),"instanceName":"85"});
            var Q86;
            Q86=makeQuery(id+"F7.opPattern","COPY",BODY,{"derivedFrom":makeQuery(id+"F3.opExtrude","SWEPT_BODY",BODY,{"disambiguationData":[OSD([sQuery(id+"F1.wireOp",EDGE,"E0"),sQuery(id+"F1.wireOp",EDGE,"E3"),sQuery(id+"F1.wireOp",EDGE,"E5"),sQuery(id+"F1.wireOp",EDGE,"E8.MirrorCS")])]}),"instanceName":"86"});
            var Q87;
            Q87=makeQuery(id+"F7.opPattern","COPY",BODY,{"derivedFrom":makeQuery(id+"F3.opExtrude","SWEPT_BODY",BODY,{"disambiguationData":[OSD([sQuery(id+"F1.wireOp",EDGE,"E0"),sQuery(id+"F1.wireOp",EDGE,"E3"),sQuery(id+"F1.wireOp",EDGE,"E5"),sQuery(id+"F1.wireOp",EDGE,"E8.MirrorCS")])]}),"instanceName":"87"});
            var Q88;
            Q88=makeQuery(id+"F7.opPattern","COPY",BODY,{"derivedFrom":makeQuery(id+"F3.opExtrude","SWEPT_BODY",BODY,{"disambiguationData":[OSD([sQuery(id+"F1.wireOp",EDGE,"E0"),sQuery(id+"F1.wireOp",EDGE,"E3"),sQuery(id+"F1.wireOp",EDGE,"E5"),sQuery(id+"F1.wireOp",EDGE,"E8.MirrorCS")])]}),"instanceName":"88"});
            var Q89;
            Q89=makeQuery(id+"F7.opPattern","COPY",BODY,{"derivedFrom":makeQuery(id+"F3.opExtrude","SWEPT_BODY",BODY,{"disambiguationData":[OSD([sQuery(id+"F1.wireOp",EDGE,"E0"),sQuery(id+"F1.wireOp",EDGE,"E3"),sQuery(id+"F1.wireOp",EDGE,"E5"),sQuery(id+"F1.wireOp",EDGE,"E8.MirrorCS")])]}),"instanceName":"89"});
            var Q90;
            Q90=makeQuery(id+"F6.opExtrude","SWEPT_BODY",BODY,{"disambiguationData":[OSD([sQuery(id+"F2.wireOp",EDGE,"E10")])]});
            booleanBodies(context, id + "F8", {"operationType" : BooleanOperationType.SUBTRACTION, "tools" : qUnion([Q0, Q1, Q2, Q3, Q4, Q5, Q6, Q7, Q8, Q9, Q10, Q11, Q12, Q13, Q14, Q15, Q16, Q17, Q18, Q19, Q20, Q21, Q22, Q23, Q24, Q25, Q26, Q27, Q28, Q29, Q30, Q31, Q32, Q33, Q34, Q35, Q36, Q37, Q38, Q39, Q40, Q41, Q42, Q43, Q44, Q45, Q46, Q47, Q48, Q49, Q50, Q51, Q52, Q53, Q54, Q55, Q56, Q57, Q58, Q59, Q60, Q61, Q62, Q63, Q64, Q65, Q66, Q67, Q68, Q69, Q70, Q71, Q72, Q73, Q74, Q75, Q76, Q77, Q78, Q79, Q80, Q81, Q82, Q83, Q84, Q85, Q86, Q87, Q88, Q89]), "targets" : qUnion([Q90])});
        }
        {
            var Q0;
            Q0=makeQuery(id+"F6.opExtrude","CAP_FACE",FACE,{"disambiguationData":[OSD([sQuery(id+"F2.wireOp",EDGE,"E10")])],"isStart":true});
            var sketch = newSketch(context, id + "F9", { "sketchPlane" : qUnion([Q0])});
            skCircle(sketch, "E12", {"center": v(0, 0) * mm, "radius": 3.17 * mm});
            skCircle(sketch, "E13", {"center": v(0, 0) * mm, "radius": 13.17 * mm});
            skCircle(sketch, "E14", {"center": v(0, 0) * mm, "radius": 7.07 * mm});
            skLineSegment(sketch, "E15", {"start": v(0, 0) * mm, "end": v(0, 7.07) * mm, "construction": true});
            skLineSegment(sketch, "E16.0", {"start": v(5, 0) * mm, "end": v(5, 5) * mm});
            skLineSegment(sketch, "E17", {"start": v(0, 0) * mm, "end": v(14.78, -8.53) * mm, "construction": true});
            skLineSegment(sketch, "E18.0", {"start": v(2.5, 4.33) * mm, "end": v(16.63, -3.83) * mm});
            skCircle(sketch, "E19", {"center": v(0, 0) * mm, "radius": 17.07 * mm});
            skSolve(sketch);
        }
        {
            var Q0;
            Q0=makeQuery(id+"F9.imprint","IMPRINT",FACE,{"disambiguationData":[TD([[makeQuery(id+"F9.imprint","IMPRINT",EDGE,{"derivedFrom":sQuery(id+"F9.wireOp",EDGE,"E12")}),1.0]])]});
            extrude(context, id + "F10", {"entities" : qUnion([Q0]), "operationType" : NewBodyOperationType.REMOVE, "oppositeDirection" : true, "depth" : 25 * mm});
        }
    });
